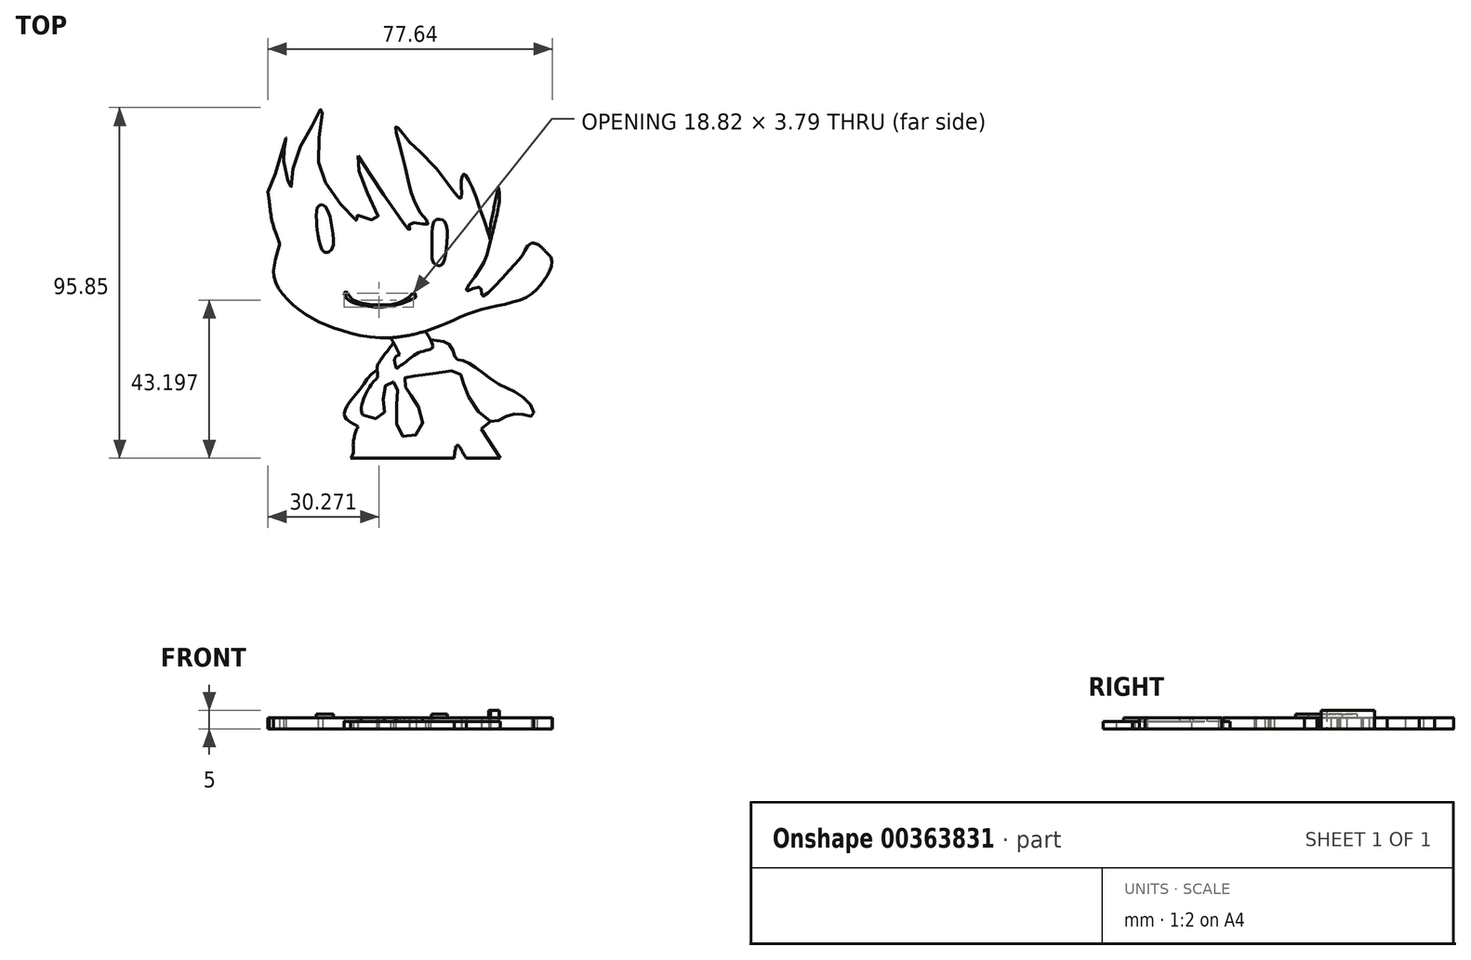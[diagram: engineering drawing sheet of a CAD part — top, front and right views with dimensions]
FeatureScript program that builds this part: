
annotation { "Feature Type Name" : "Feature", "Feature Type Description" : "" }
export const myFeature = defineFeature(function(context is Context, id is Id, definition is map)
    precondition{}
    {
        {
            var Q0;
            Q0=qCreatedBy(makeId("Top.planeOp"),FACE);
            var sketch = newSketch(context, id + "F0", { "sketchPlane" : qUnion([Q0])});
            skFitSpline(sketch, "E0", {"points": [v(-35.63, -8.2) * mm, v(-36.57, -11.8) * mm, v(-37.2, -16.36) * mm, v(-34.53, -21.85) * mm, v(-27.94, -27.5) * mm, v(-20.1, -31.1) * mm, v(-6.91, -33.62) * mm, v(8, -30.48) * mm, v(19.3, -25.93) * mm, v(32.16, -22.32) * mm, v(37.65, -16.36) * mm, v(38.6, -11.5) * mm, v(33.26, -7.73) * mm, v(31.06, -10.55) * mm, v(26.98, -15.42) * mm, v(19.76, -22.17) * mm, v(19.3, -19.81) * mm, v(15.52, -20.75) * mm, v(19.13, -14.95) * mm, v(22.12, -6.94) * mm, v(24.47, 4.04) * mm, v(24.16, 7.65) * mm], "startDerivative": vector(-26.47, -102.66) * mm, "endDerivative": vector(-19.51, 89.57) * mm});
            skFitSpline(sketch, "E1", {"points": [v(22.12, -6.94) * mm, v(14.9, 11.1) * mm, v(14.11, 9.38) * mm, v(13.96, 4.51) * mm, v(8.15, 11.57) * mm, v(0, 19.89) * mm], "startDerivative": vector(-28.54, 86.32) * mm, "endDerivative": vector(-29.73, 29.86) * mm});
            skFitSpline(sketch, "E2", {"points": [v(0, 19.89) * mm, v(-3.78, 24.13) * mm, v(-1.9, 15.8) * mm, v(2.34, 1.53) * mm, v(4.85, -2.55) * mm, v(0, -2.4) * mm, v(0, -4.12) * mm, v(-14.13, 16.12) * mm], "startDerivative": vector(-42.01, 55.94) * mm, "endDerivative": vector(-84.27, 126.95) * mm});
            skFitSpline(sketch, "E3", {"points": [v(-14.13, 16.12) * mm, v(-12.93, 8.92) * mm, v(-8.75, -1.77) * mm, v(-14.13, 0) * mm, v(-14.13, -1.64) * mm, v(-21.57, 6.46) * mm, v(-24.98, 18.4) * mm, v(-23.88, 29.34) * mm, v(-26.14, 25.34) * mm, v(-31.88, 13.07) * mm, v(-32.52, 7.33) * mm, v(-34.31, 14.06) * mm, v(-34.26, 18.18) * mm, v(-33.8, 21.07) * mm, v(-36.13, 12.94) * mm, v(-40.03, 3.98) * mm, v(-42.68, 1.08) * mm, v(-41.96, 10.82) * mm, v(-41.6, 22.57) * mm, v(-43.19, 14.79) * mm, v(-43.7, 11.25) * mm, v(-45.64, 19.38) * mm, v(-44.56, 28.13) * mm, v(-39.02, 42.18) * mm, v(-27.94, 51.62) * mm, v(-17.28, 58.06) * mm, v(-10.95, 60.07) * mm], "startDerivative": vector(-5.86, -160.26) * mm, "endDerivative": vector(170.43, 50.75) * mm});
            skFitSpline(sketch, "E4", {"points": [v(11.11, 60.7) * mm, v(19.94, 58.04) * mm, v(25.25, 54.57) * mm, v(30.92, 51.26) * mm, v(37.5, 45.62) * mm, v(42.69, 38.53) * mm, v(45.32, 32.41) * mm, v(47.37, 27.9) * mm, v(48.02, 21.03) * mm, v(48.47, 14.66) * mm, v(47.24, 3.83) * mm, v(45.74, -2.4) * mm, v(44.6, 0) * mm, v(40.03, -7.98) * mm, v(38.6, -11.5) * mm, v(33.26, -7.73) * mm], "startDerivative": vector(122.7, -27.86) * mm, "endDerivative": vector(-118.01, -12.52) * mm});
            skFitSpline(sketch, "E5", {"points": [v(24.16, 7.65) * mm, v(21.58, -5.32) * mm], "startDerivative": vector(-2.6, -12.97) * mm, "endDerivative": vector(-2.6, -12.97) * mm});
            skFitSpline(sketch, "E6", {"points": [v(-38.4, 3.98) * mm, v(-37.1, -3.5) * mm, v(-35.63, -8.2) * mm, v(-37.38, -6.4) * mm, v(-38.87, 0) * mm, v(-38.12, 1.25) * mm], "startDerivative": vector(2.64, -27.2) * mm, "endDerivative": vector(8.06, 7.6) * mm});
            skFitSpline(sketch, "E7", {"points": [v(-5.25, -33.57) * mm, v(-4.43, -34.93) * mm, v(-2.75, -38.2) * mm], "startDerivative": vector(1.94, -3.04) * mm, "endDerivative": vector(3, -6.02) * mm});
            skFitSpline(sketch, "E8", {"points": [v(-3.68, -41.93) * mm, v(-4.05, -39.13) * mm, v(-2.75, -38.2) * mm], "startDerivative": vector(-1.7, 5.7) * mm, "endDerivative": vector(3.83, 1.58) * mm});
            skFitSpline(sketch, "E9", {"points": [v(4.23, -31.8) * mm, v(6.21, -36.33) * mm, v(2.95, -37.45) * mm, v(-1.16, -40.25) * mm, v(-3.68, -41.93) * mm], "startDerivative": vector(13.2, -20.24) * mm, "endDerivative": vector(-11.2, -6.68) * mm});
            skFitSpline(sketch, "E10", {"points": [v(5.64, -34.06) * mm, v(8.3, -34.5) * mm, v(10.6, -35.18) * mm, v(12.05, -37.7) * mm, v(12.63, -39.35) * mm, v(14.2, -39.73) * mm, v(16.39, -40.68) * mm, v(19.73, -43) * mm, v(24.5, -46.37) * mm, v(28.75, -48.4) * mm, v(33.23, -52.32) * mm, v(33.6, -54.93) * mm, v(30.15, -54.37) * mm, v(25.95, -55.3) * mm, v(22.03, -56.42) * mm, v(16.06, -49.7) * mm, v(14.29, -44.66) * mm, v(12.89, -42.8) * mm, v(2.53, -43.92) * mm, v(-1.3, -44.57) * mm, v(-0.92, -47.56) * mm, v(1.32, -50.73) * mm, v(3.28, -58.38) * mm, v(-1.76, -60.62) * mm, v(-3.68, -52.5) * mm, v(-3.68, -46.34) * mm, v(-5.68, -45.7) * mm, v(-7.27, -50.36) * mm, v(-7.45, -55.02) * mm, v(-12.86, -54.65) * mm, v(-10.06, -45.78) * mm, v(-8.76, -44.2) * mm, v(-8.95, -41.93) * mm, v(-7.92, -39.63) * mm, v(-4.43, -34.93) * mm], "startDerivative": vector(114.11, -20.45) * mm, "endDerivative": vector(113, 148.55) * mm});
            skFitSpline(sketch, "E11", {"points": [v(-8.93, -42.33) * mm, v(-10.83, -43.92) * mm, v(-12.6, -46.35) * mm, v(-16.22, -50.95) * mm, v(-17.82, -54.95) * mm, v(-15.6, -57) * mm, v(-14.16, -57.83) * mm], "startDerivative": vector(-13.9, -10.14) * mm, "endDerivative": vector(10.6, -6.1) * mm});
            skFitSpline(sketch, "E12", {"points": [v(-12.86, -54.65) * mm, v(-14.16, -57.83) * mm, v(-15.45, -62.62) * mm, v(-16.2, -66.44) * mm, v(-20.67, -66.72) * mm, v(-19.18, -64.3) * mm, v(-18.15, -61.13) * mm, v(-16.8, -57.83) * mm, v(-16.14, -56.68) * mm], "startDerivative": vector(-9.85, -23.85) * mm, "endDerivative": vector(7.64, 12.43) * mm});
            skFitSpline(sketch, "E13", {"points": [v(12.12, -66.44) * mm, v(13.06, -62.95) * mm, v(14.69, -65.28) * mm, v(15.44, -66.5) * mm], "startDerivative": vector(1.56, 13.33) * mm, "endDerivative": vector(2.5, -3.67) * mm});
            skLineSegment(sketch, "E14", {"start": v(15.44, -66.5) * mm, "end": v(24.72, -66.5) * mm});
            skLineSegment(sketch, "E15", {"start": v(24.72, -66.5) * mm, "end": v(19.54, -58.51) * mm});
            skLineSegment(sketch, "E16", {"start": v(19.54, -58.51) * mm, "end": v(22.03, -56.42) * mm});
            skLineSegment(sketch, "E17", {"start": v(-10.95, 60.07) * mm, "end": v(-59.9, 60.07) * mm});
            skLineSegment(sketch, "E18", {"start": v(-59.9, 60.07) * mm, "end": v(-59.9, -67.93) * mm});
            skLineSegment(sketch, "E19", {"start": v(-59.9, -67.93) * mm, "end": v(66.1, -67.93) * mm});
            skLineSegment(sketch, "E20", {"start": v(66.1, -67.93) * mm, "end": v(66.1, 60.07) * mm});
            skFitSpline(sketch, "E21", {"points": [v(-23.88, 2.87) * mm, v(-24.89, 2.47) * mm, v(-25.41, 1.48) * mm, v(-25.46, -1.28) * mm, v(-25.33, -3.59) * mm, v(-24.8, -6.83) * mm, v(-24.11, -9.24) * mm, v(-22.9, -10.4) * mm, v(-21.3, -9.46) * mm, v(-20.88, -6.4) * mm, v(-21.34, -2.55) * mm, v(-22.21, 0.87) * mm, v(-23.88, 2.87) * mm]});
            skFitSpline(sketch, "E22", {"points": [v(6.05, -6.7) * mm, v(6.05, -9.88) * mm, v(6.36, -13) * mm, v(7.97, -13.88) * mm, v(9.15, -13.26) * mm, v(10.13, -8.18) * mm, v(10.15, -3.5) * mm, v(9.26, -1.53) * mm, v(7.97, -1.15) * mm, v(6.65, -1.78) * mm, v(6.05, -6.7) * mm]});
            skFitSpline(sketch, "E23", {"points": [v(-17.87, -21.44) * mm, v(-17.42, -22.64) * mm, v(-16.44, -23.52) * mm, v(-14.87, -24.24) * mm, v(-11.38, -25) * mm, v(-7.8, -25.19) * mm, v(-3.4, -24.62) * mm, v(0, -23.4) * mm, v(1.63, -22.48) * mm, v(1.7, -21.64) * mm, v(1.02, -21.38) * mm, v(0.47, -21.77) * mm, v(0, -22.34) * mm, v(-0.79, -22.99) * mm, v(-2.65, -23.93) * mm, v(-5.36, -24.54) * mm, v(-10.28, -24.56) * mm, v(-14, -23.9) * mm, v(-16.58, -22.46) * mm, v(-16.81, -21.42) * mm, v(-17.38, -21.07) * mm, v(-17.83, -21.22) * mm, v(-17.87, -21.44) * mm]});
            skLineSegment(sketch, "E24", {"start": v(-10.95, 60.07) * mm, "end": v(11.11, 60.7) * mm});
            skFitSpline(sketch, "E25", {"points": [v(-38.4, 3.98) * mm, v(-38.73, 6.24) * mm], "startDerivative": vector(-0.34, 2.27) * mm, "endDerivative": vector(-0.34, 2.27) * mm});
            skLineSegment(sketch, "E26", {"start": v(-16.2, -66.44) * mm, "end": v(12.12, -66.44) * mm});
            skLineSegment(sketch, "E27", {"start": v(-73.52, 69.8) * mm, "end": v(-73.52, -70.95) * mm});
            skLineSegment(sketch, "E28", {"start": v(-73.52, -70.95) * mm, "end": v(74.27, -70.95) * mm});
            skLineSegment(sketch, "E29", {"start": v(74.27, 69.8) * mm, "end": v(74.27, -70.95) * mm});
            skLineSegment(sketch, "E30", {"start": v(74.27, 69.8) * mm, "end": v(-73.52, 69.8) * mm});
            skSolve(sketch);
        }
        {
            var Q0;
            Q0=makeQuery(id+"F0.imprint","IMPRINT",FACE,{"disambiguationData":[TD([[makeQuery(id+"F0.imprint","IMPRINT",EDGE,{"derivedFrom":sQuery(id+"F0.wireOp",EDGE,"E1")}),-1.0]])]});
            extrude(context, id + "F1", {"entities" : qUnion([Q0]), "depth" : 5 * mm});
        }
        {
            var Q0;
            Q0=makeQuery(id+"F0.imprint","IMPRINT",FACE,{"disambiguationData":[TD([[makeQuery(id+"F0.imprint","IMPRINT",EDGE,{"derivedFrom":sQuery(id+"F0.wireOp",EDGE,"E1")}),1.0]])]});
            extrude(context, id + "F2", {"entities" : qUnion([Q0]), "depth" : 3 * mm});
        }
        {
            var Q0;
            Q0=makeQuery(id+"F0.imprint","IMPRINT",FACE,{"disambiguationData":[TD([[makeQuery(id+"F0.imprint","IMPRINT",EDGE,{"derivedFrom":sQuery(id+"F0.wireOp",EDGE,"E22")}),1.0]])]});
            var Q1;
            Q1=makeQuery(id+"F0.imprint","IMPRINT",FACE,{"disambiguationData":[TD([[makeQuery(id+"F0.imprint","IMPRINT",EDGE,{"derivedFrom":sQuery(id+"F0.wireOp",EDGE,"E21")}),1.0]])]});
            extrude(context, id + "F3", {"entities" : qUnion([Q0, Q1]), "operationType" : NewBodyOperationType.ADD, "depth" : 4 * mm});
        }
        {
            var Q0;
            {var subQ0=sQuery(id+"F0.wireOp",EDGE,"E8");Q0=makeQuery(id+"F0.imprint","IMPRINT",FACE,{"disambiguationData":[TD([[makeQuery(id+"F0.imprint","IMPRINT",EDGE,{"derivedFrom":subQ0}),-1.0]])]});}
            extrude(context, id + "F4", {"entities" : qUnion([Q0]), "depth" : 2 * mm});
        }
        {
            var Q0;
            {var subQ4=sQuery(id+"F0.wireOp",EDGE,"E8");Q0=makeQuery(id+"F0.imprint","IMPRINT",FACE,{"disambiguationData":[TD([[makeQuery(id+"F0.imprint","IMPRINT",EDGE,{"derivedFrom":subQ4}),1.0]])]});}
            extrude(context, id + "F5", {"entities" : qUnion([Q0]), "operationType" : NewBodyOperationType.ADD, "depth" : 3 * mm});
        }
        {
            var Q0;
            {var subQ0=sQuery(id+"F0.wireOp",EDGE,"E11");Q0=makeQuery(id+"F0.imprint","IMPRINT",FACE,{"disambiguationData":[TD([[makeQuery(id+"F0.imprint","IMPRINT",EDGE,{"derivedFrom":subQ0}),1.0]])]});}
            var Q1;
            Q1=makeQuery(id+"F0.imprint","IMPRINT",FACE,{"disambiguationData":[TD([[makeQuery(id+"F0.imprint","IMPRINT",EDGE,{"derivedFrom":sQuery(id+"F0.wireOp",EDGE,"E13")}),1.0]])]});
            extrude(context, id + "F6", {"entities" : qUnion([Q0, Q1]), "operationType" : NewBodyOperationType.ADD, "depth" : 2 * mm});
        }
    });
